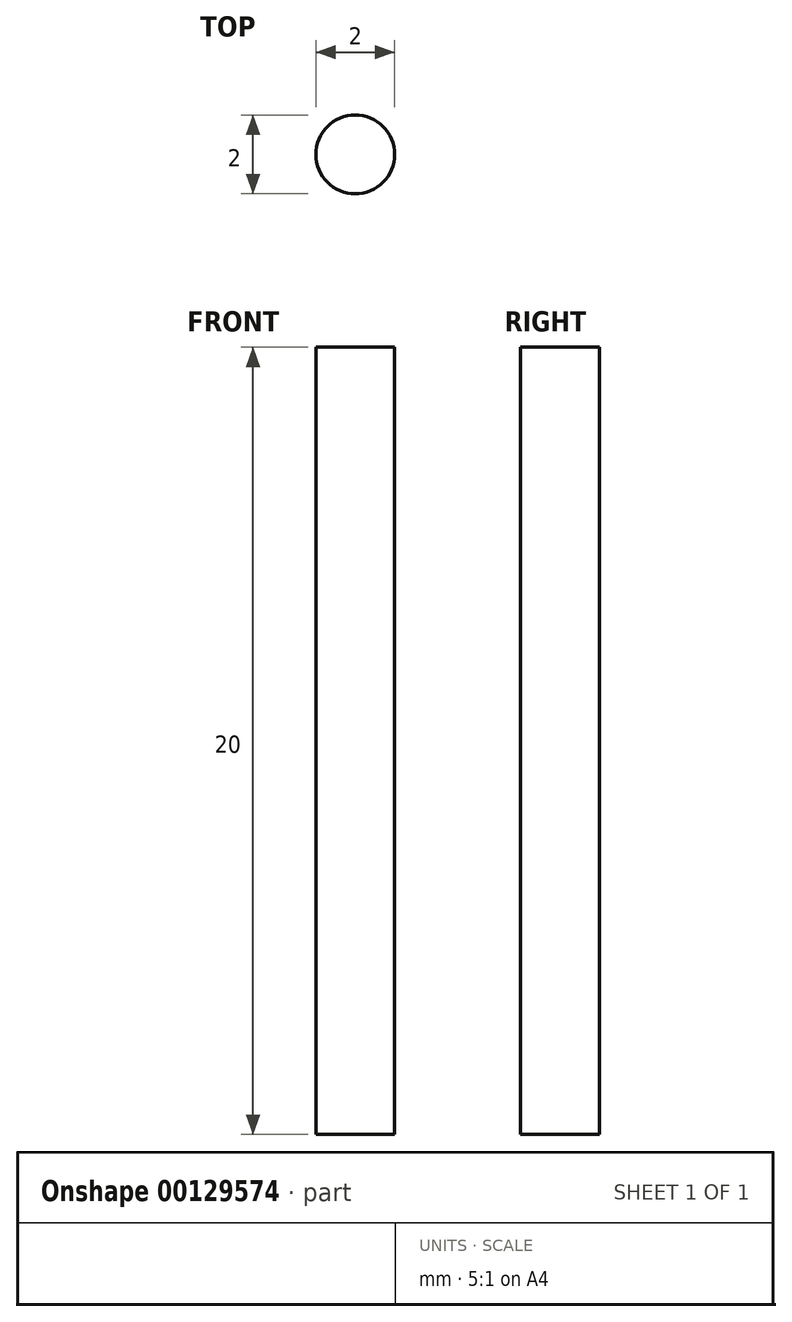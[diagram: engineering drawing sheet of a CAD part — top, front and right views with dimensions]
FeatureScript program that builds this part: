
annotation { "Feature Type Name" : "Feature", "Feature Type Description" : "" }
export const myFeature = defineFeature(function(context is Context, id is Id, definition is map)
    precondition{}
    {
        {
            var Q0;
            Q0=qCreatedBy(makeId("Top.planeOp"),FACE);
            var sketch = newSketch(context, id + "F0", { "sketchPlane" : qUnion([Q0])});
            skCircle(sketch, "E0", {"center": v(0, 0) * mm, "radius": 1 * mm});
            skSolve(sketch);
        }
        {
            var Q0;
            Q0 = qSketchRegion(id + "F0", true);
            extrude(context, id + "F1", {"entities" : qUnion([Q0]), "depth" : 20 * mm});
        }
    });
